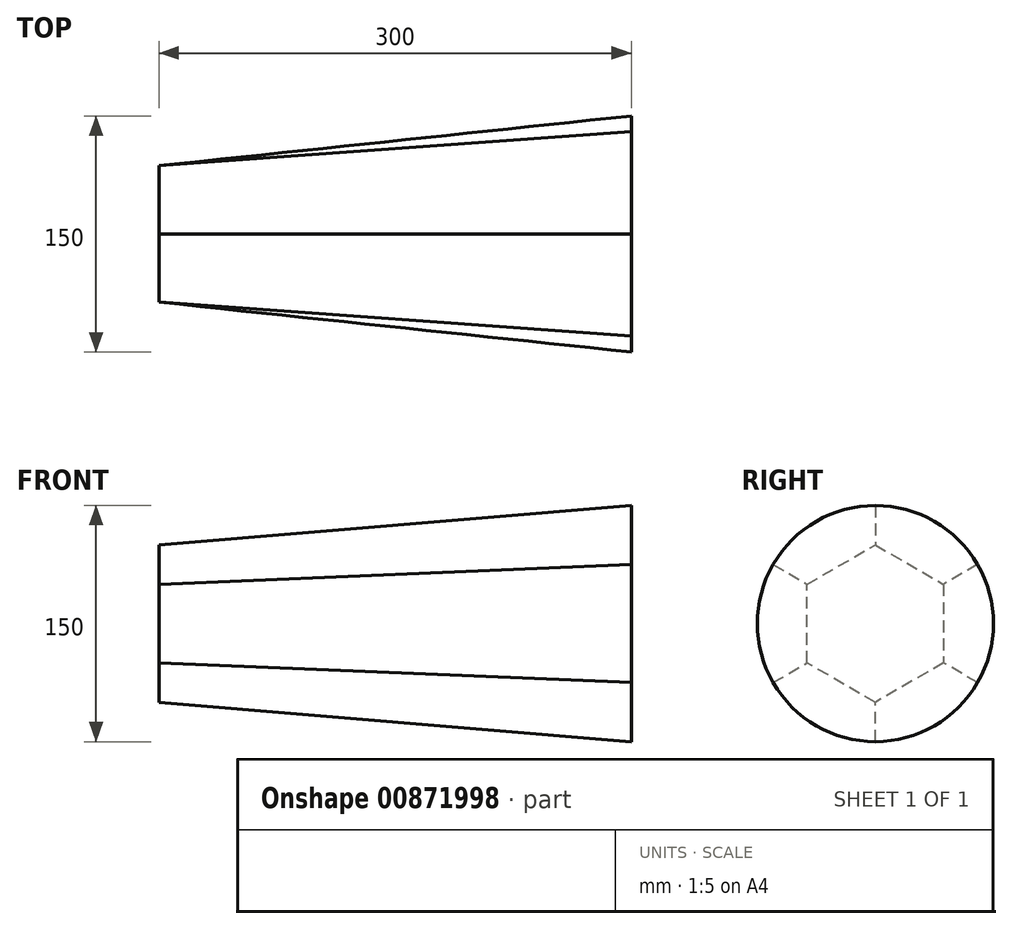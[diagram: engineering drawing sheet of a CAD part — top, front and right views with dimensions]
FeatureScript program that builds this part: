
annotation { "Feature Type Name" : "Feature", "Feature Type Description" : "" }
export const myFeature = defineFeature(function(context is Context, id is Id, definition is map)
    precondition{}
    {
        {
            var Q0;
            Q0=qCreatedBy(makeId("Right.planeOp"),FACE);
            var sketch = newSketch(context, id + "F0", { "sketchPlane" : qUnion([Q0])});
            skCircle(sketch, "E0", {"center": v(0, 0) * mm, "radius": 75 * mm});
            skSolve(sketch);
        }
        {
            var Q0;
            Q0=qCreatedBy(makeId("Right.planeOp"),FACE);
            cPlane(context, id + "F1", {"entities" : qUnion([Q0]), "cplaneType" : CPlaneType.OFFSET, "offset" : 300 * mm, "oppositeDirection" : true, "width" : 150 * mm, "height" : 150 * mm});
        }
        {
            var Q0;
            Q0=qCreatedBy(id+"F1.planeOp",FACE);
            var sketch = newSketch(context, id + "F2", { "sketchPlane" : qUnion([Q0])});
            skCircle(sketch, "E1.cCircle", {"center": v(0, 0) * mm, "radius": 50 * mm, "construction": true});
            skLineSegment(sketch, "E1.0", {"start": v(0, 50) * mm, "end": v(43.3, 25) * mm});
            skLineSegment(sketch, "E1.1", {"start": v(43.3, 25) * mm, "end": v(43.3, -25) * mm});
            skLineSegment(sketch, "E1.2", {"start": v(43.3, -25) * mm, "end": v(0, -50) * mm});
            skLineSegment(sketch, "E1.3", {"start": v(0, -50) * mm, "end": v(-43.3, -25) * mm});
            skLineSegment(sketch, "E1.4", {"start": v(-43.3, -25) * mm, "end": v(-43.3, 25) * mm});
            skLineSegment(sketch, "E1.5", {"start": v(-43.3, 25) * mm, "end": v(0, 50) * mm});
            skSolve(sketch);
        }
        {
            var Q0;
            Q0 = qSketchRegion(id + "F0", true);
            var Q1;
            Q1 = qSketchRegion(id + "F2", true);
            loft(context, id + "F3", {"sheetProfilesArray" : [{ "sheetProfileEntities" : qUnion([Q0]) }, { "sheetProfileEntities" : qUnion([Q1]) }]});
        }
    });
